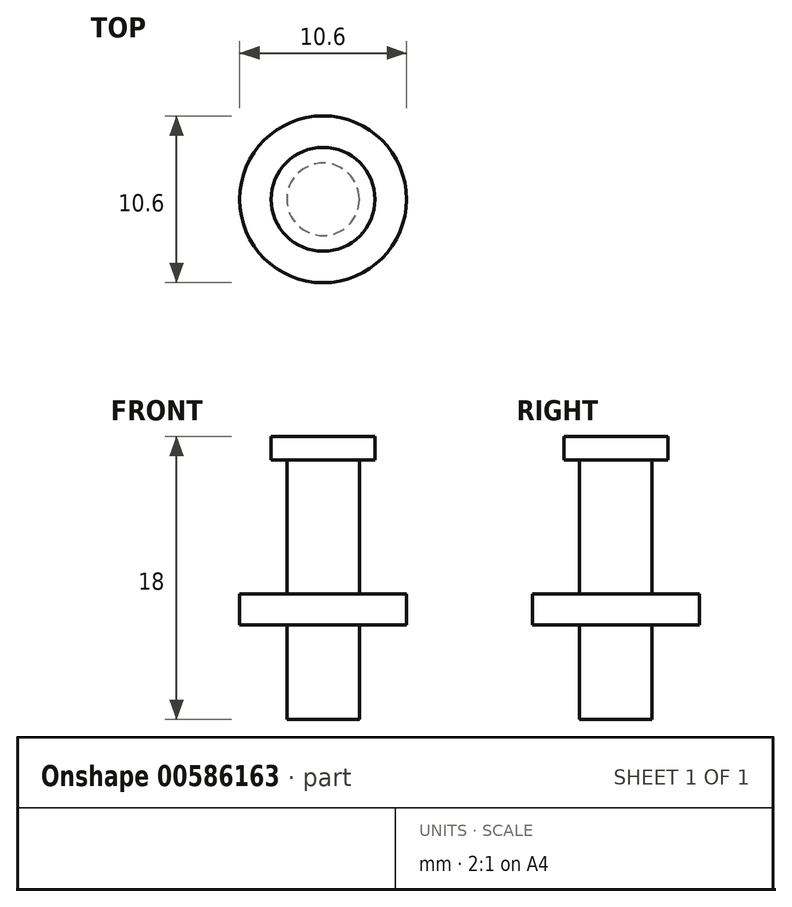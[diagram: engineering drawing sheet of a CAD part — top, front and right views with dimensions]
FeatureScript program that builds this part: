
annotation { "Feature Type Name" : "Feature", "Feature Type Description" : "" }
export const myFeature = defineFeature(function(context is Context, id is Id, definition is map)
    precondition{}
    {
        {
            var Q0;
            Q0=qCreatedBy(makeId("Top.planeOp"),FACE);
            var sketch = newSketch(context, id + "F0", { "sketchPlane" : qUnion([Q0])});
            skCircle(sketch, "E0", {"center": v(-7.5, 0) * mm, "radius": 2.3 * mm});
            skLineSegment(sketch, "E1.bottom", {"start": v(-15, 5.3) * mm, "end": v(0, 5.3) * mm});
            skLineSegment(sketch, "E1.top", {"start": v(-15, -5.3) * mm, "end": v(0, -5.3) * mm});
            skLineSegment(sketch, "E1.left", {"start": v(-15, 5.3) * mm, "end": v(-15, -5.3) * mm});
            skLineSegment(sketch, "E1.right", {"start": v(0, 5.3) * mm, "end": v(0, -5.3) * mm});
            skLineSegment(sketch, "E2.direction1", {"start": v(-15, -5.3) * mm, "end": v(0, -5.3) * mm, "construction": true});
            skCircle(sketch, "E3", {"center": v(-7.5, 0) * mm, "radius": 5.3 * mm});
            skCircle(sketch, "E4", {"center": v(-7.5, 0) * mm, "radius": 3.3 * mm});
            skSolve(sketch);
        }
        {
            var Q0;
            Q0=makeQuery(id+"F0.imprint","IMPRINT",FACE,{"disambiguationData":[TD([[makeQuery(id+"F0.imprint","IMPRINT",EDGE,{"derivedFrom":sQuery(id+"F0.wireOp",EDGE,"E4")}),-1.0]])]});
            var Q1;
            Q1=makeQuery(id+"F0.imprint","IMPRINT",FACE,{"disambiguationData":[TD([[makeQuery(id+"F0.imprint","IMPRINT",EDGE,{"derivedFrom":sQuery(id+"F0.wireOp",EDGE,"E0")}),-1.0]])]});
            extrude(context, id + "F1", {"entities" : qUnion([Q0, Q1]), "oppositeDirection" : true, "depth" : 2 * mm, "offsetDistance" : 25 * mm});
        }
        {
            var Q0;
            Q0=makeQuery(id+"F0.imprint","IMPRINT",FACE,{"disambiguationData":[TD([[makeQuery(id+"F0.imprint","IMPRINT",EDGE,{"derivedFrom":sQuery(id+"F0.wireOp",EDGE,"E0")}),1.0]])]});
            extrude(context, id + "F2", {"entities" : qUnion([Q0]), "operationType" : NewBodyOperationType.ADD, "depth" : 10 * mm, "offsetDistance" : 25 * mm, "hasSecondDirection" : true, "secondDirectionOppositeDirection" : true, "secondDirectionDepth" : 8 * mm});
        }
        {
            var Q0;
            Q0=makeQuery(id+"F0.imprint","IMPRINT",FACE,{"disambiguationData":[TD([[makeQuery(id+"F0.imprint","IMPRINT",EDGE,{"derivedFrom":sQuery(id+"F0.wireOp",EDGE,"E0")}),-1.0]])]});
            extrude(context, id + "F3", {"entities" : qUnion([Q0]), "operationType" : NewBodyOperationType.ADD, "depth" : 10 * mm, "offsetDistance" : 25 * mm, "hasSecondDirection" : true, "secondDirectionOppositeDirection" : false, "secondDirectionDepth" : 8.5 * mm});
        }
    });
